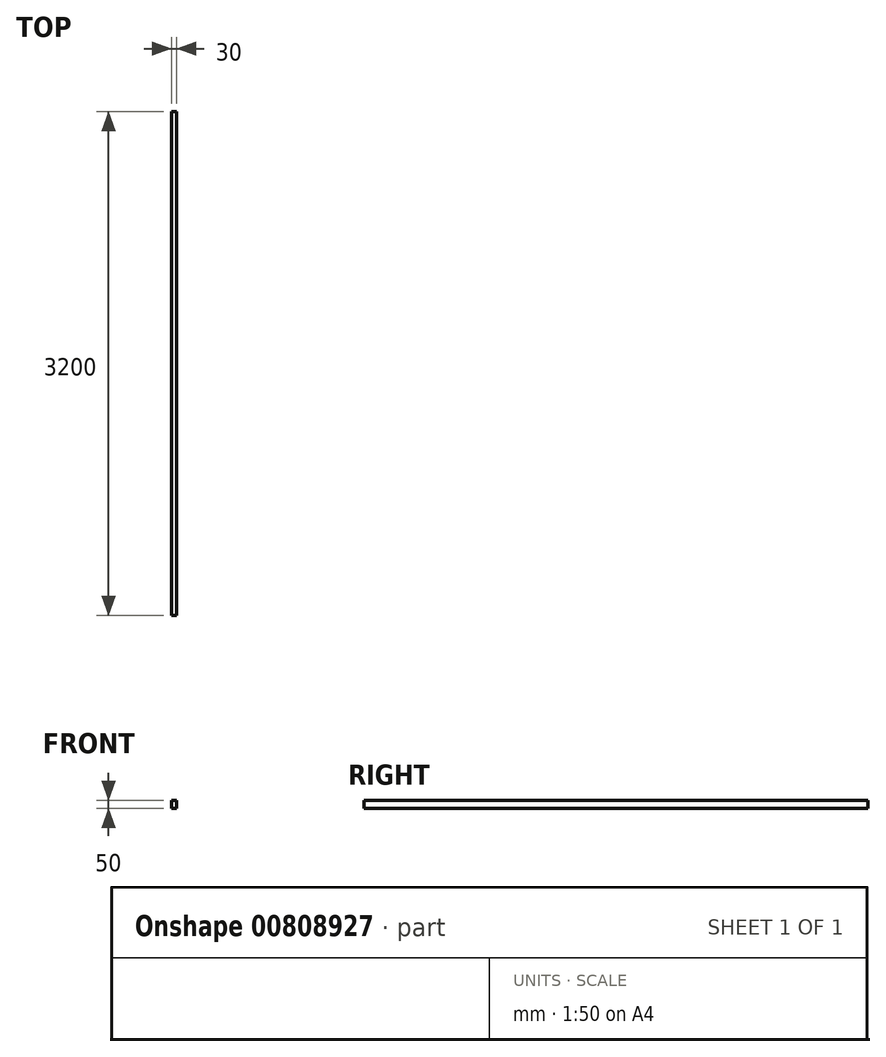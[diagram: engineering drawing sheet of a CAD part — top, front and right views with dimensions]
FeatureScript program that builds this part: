
annotation { "Feature Type Name" : "Feature", "Feature Type Description" : "" }
export const myFeature = defineFeature(function(context is Context, id is Id, definition is map)
    precondition{}
    {
        {
            var Q0;
            Q0=qCreatedBy(makeId("Front.planeOp"),FACE);
            var sketch = newSketch(context, id + "F0", { "sketchPlane" : qUnion([Q0])});
            skLineSegment(sketch, "E0.bottom", {"start": v(0, 0) * mm, "end": v(30, 0) * mm});
            skLineSegment(sketch, "E0.top", {"start": v(0, 50) * mm, "end": v(30, 50) * mm});
            skLineSegment(sketch, "E0.left", {"start": v(0, 0) * mm, "end": v(0, 50) * mm});
            skLineSegment(sketch, "E0.right", {"start": v(30, 0) * mm, "end": v(30, 50) * mm});
            skSolve(sketch);
        }
        {
            var Q0;
            Q0 = qSketchRegion(id + "F0", true);
            extrude(context, id + "F1", {"entities" : qUnion([Q0]), "oppositeDirection" : true, "depth" : 3200 * mm, "offsetDistance" : 25 * mm});
        }
    });
